# Revit family: 59TV_WaveTopTables With Bench Folded
name_source: partatom
category: Furniture
units: mm (PartAtom-declared; Revit-internal decimal feet)

## family parameters
Always vertical = Yes
Cut with Voids When Loaded = No
OmniClass Number = 23.40.20.00
OmniClass Title = General Furniture and Specialties
Room Calculation Point = No
Shared = No
Work Plane-Based = No

## types (4) — shared parameters
Caster Trim = Frame, Chrome
Glide = Glide, Black
LeftBench2 = Yes
LeftBenchStand = Yes
LeftSeat = No
Manufacturer = PalmerHamilton
RightBench1 = Yes
RightBenchStand = Yes
RightSeat = No
Type Comments = Cafeteria Table
URL = https://palmerhamilton.com
Wheel = Poly II Gray
zero-valued in all types: Default Elevation

## per-type parameters (varying)
| type | BenchFrameWidth1 | BenchFrameWidth2 | BenchTopWidth1 | BenchTopWidth2 | BushLegDistance | CLegDepth | CasterLegDistance | CenterLegDistance | ClampDistance | Description | FrameWidth | LargeRod1 | LargeRod2 | LargeTop | MiddleFrame | SeatingHeight | SmallRod1 | SmallRod2 | SmallTop | TotalHeight |
| 59TV23273012W-BNCH | 34.61 " | 23.39 " | 36.41 " | 26.18 " | 19.6 " | 7.23 " | 23.38 " | 42.22 " | 11.75 " | 12 Bench Table 12'W - 27” High | 38.82 " | No | Yes | Yes | Yes | 15.56 " | No | No | No | 27.43 " |
| 59TV23293010W-BNCH | 26.05 " | 24.9 " | 28.36 " | 26.63 " | 21.68 " | 7.62 " | 17.14 " | 46.5 " | 8.66 " | 12 Bench Table 10'W- 29” High | 26.83 " | No | No | No | No | 17.2 " | Yes | Yes | Yes | 27.23 " |
| 59TV23293012W-BNCH | 36.35 " | 21.65 " | 38.15 " | 25.44 " | 19.33 " | 7.23 " | 25.64 " | 41.7 " | 11.75 " | 12 Bench Table 12'W- 29” High | 38.82 " | Yes | Yes | Yes | Yes | 17.19 " | No | No | No | 27.23 " |
| 59TV23273010W-BNCH | 25.88 " | 24.9 " | 28.36 " | 26.63 " | 21.32 " | 7.62 " | 15.09 " | 47.5 " | 8.66 " | 12 Bench Table 10'W - 27” High | 26.83 " | No | No | No | No | 15.19 " | No | Yes | Yes | 27.23 " |

note: column(s) folded — value = type name in every type: Model

## geometry (parser evidence)
native form markers: Sweep x85
no freeform markers — native parametric forms only
